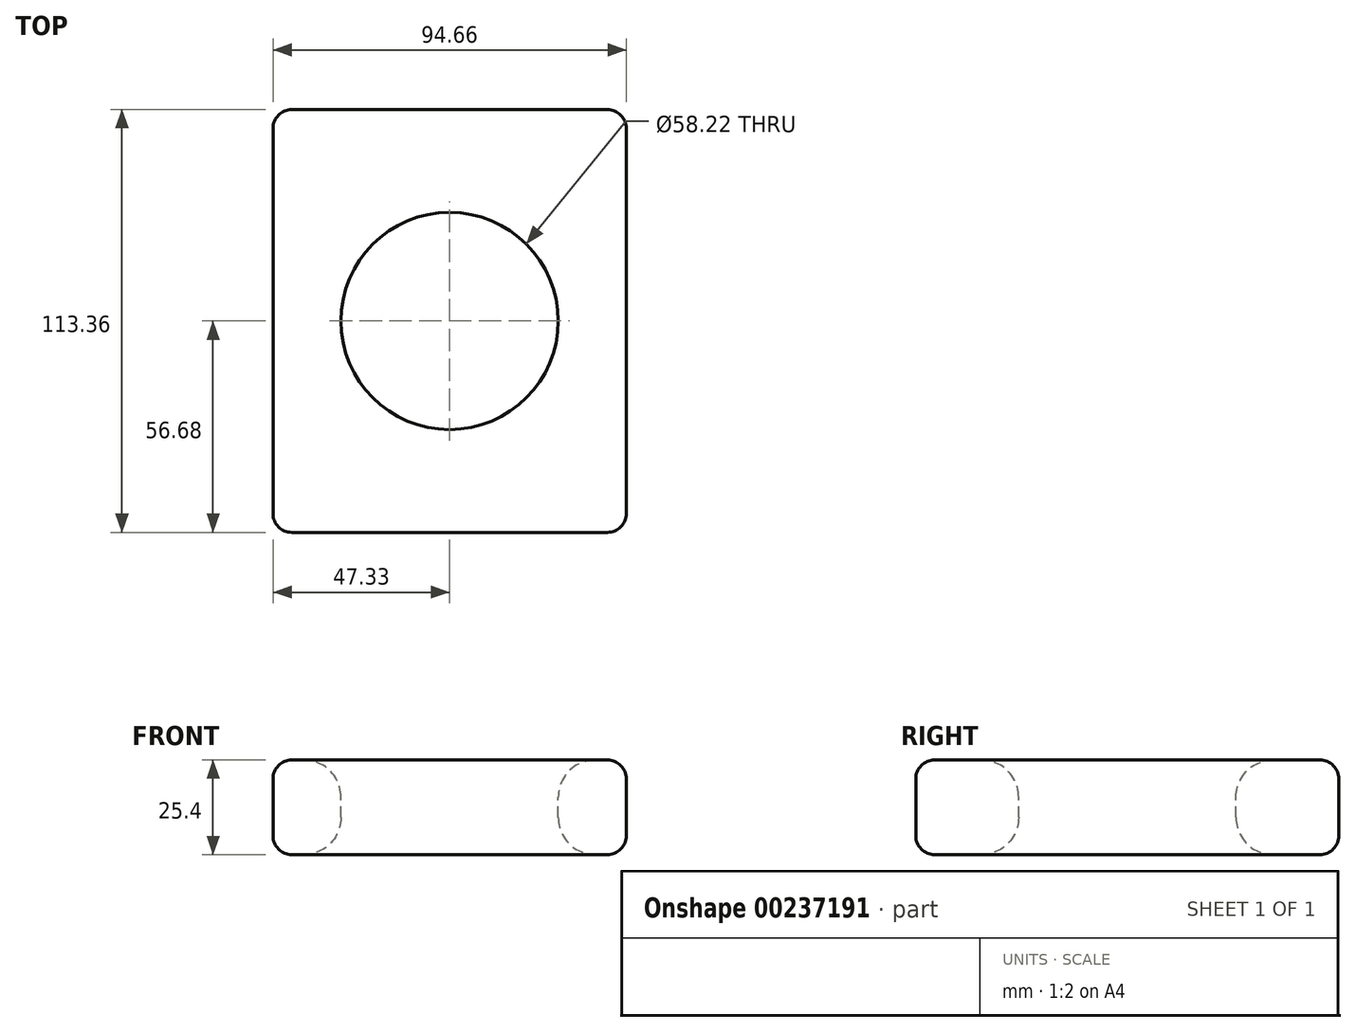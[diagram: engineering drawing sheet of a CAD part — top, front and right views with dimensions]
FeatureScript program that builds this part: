
annotation { "Feature Type Name" : "Feature", "Feature Type Description" : "" }
export const myFeature = defineFeature(function(context is Context, id is Id, definition is map)
    precondition{}
    {
        {
            var Q0;
            Q0=qCreatedBy(makeId("Top.planeOp"),FACE);
            var sketch = newSketch(context, id + "F0", { "sketchPlane" : qUnion([Q0])});
            skLineSegment(sketch, "E0.bottom", {"start": v(47.33, 56.68) * mm, "end": v(-47.33, 56.68) * mm});
            skLineSegment(sketch, "E0.top", {"start": v(47.33, -56.68) * mm, "end": v(-47.33, -56.68) * mm});
            skLineSegment(sketch, "E0.left", {"start": v(47.33, 56.68) * mm, "end": v(47.33, -56.68) * mm});
            skLineSegment(sketch, "E0.right", {"start": v(-47.33, 56.68) * mm, "end": v(-47.33, -56.68) * mm});
            skPoint(sketch, "E0.middle", {"position": v(0, 0) * mm});
            skSolve(sketch);
        }
        {
            var Q0;
            Q0=makeQuery(id+"F0.imprint","IMPRINT",FACE,{"disambiguationData":[TD([[makeQuery(id+"F0.imprint","IMPRINT",EDGE,{"derivedFrom":sQuery(id+"F0.wireOp",EDGE,"E0.bottom")}),1.0]])]});
            extrude(context, id + "F1", {"entities" : qUnion([Q0]), "depth" : 25.4 * mm});
        }
        {
            var Q0;
            Q0=makeQuery(id+"F1.opExtrude","CAP_FACE",FACE,{"disambiguationData":[OSD([sQuery(id+"F0.wireOp",EDGE,"E0.bottom"),sQuery(id+"F0.wireOp",EDGE,"E0.top"),sQuery(id+"F0.wireOp",EDGE,"E0.left"),sQuery(id+"F0.wireOp",EDGE,"E0.right")])],"isStart":false});
            var sketch = newSketch(context, id + "F2", { "sketchPlane" : qUnion([Q0])});
            skCircle(sketch, "E1", {"center": v(0, 0) * mm, "radius": 29.1 * mm});
            skSolve(sketch);
        }
        {
            var Q0;
            Q0 = qSketchRegion(id + "F2", true);
            extrude(context, id + "F3", {"entities" : qUnion([Q0]), "operationType" : NewBodyOperationType.REMOVE, "endBound" : BoundingType.THROUGH_ALL, "oppositeDirection" : true, "depth" : 25.4 * mm});
        }
        {
            var Q0;
            Q0=makeQuery(id+"F1.opExtrude","SWEPT_FACE",FACE,{"disambiguationData":[OSD([sQuery(id+"F0.wireOp",EDGE,"E0.top")])]});
            var Q1;
            Q1=makeQuery(id+"F1.opExtrude","SWEPT_FACE",FACE,{"disambiguationData":[OSD([sQuery(id+"F0.wireOp",EDGE,"E0.left")])]});
            var Q2;
            Q2=makeQuery(id+"F1.opExtrude","SWEPT_FACE",FACE,{"disambiguationData":[OSD([sQuery(id+"F0.wireOp",EDGE,"E0.bottom")])]});
            var Q3;
            Q3=makeQuery(id+"F1.opExtrude","SWEPT_FACE",FACE,{"disambiguationData":[OSD([sQuery(id+"F0.wireOp",EDGE,"E0.right")])]});
            fillet(context, id + "F4", {"entities" : qUnion([Q0, Q1, Q2, Q3]), "radius" : 5.08 * mm, "tangentPropagation" : true, "allowEdgeOverflow" : false});
        }
        {
            var Q0;
            Q0=makeQuery(id+"F3.boolean.opBoolean","COPY",FACE,{"derivedFrom":makeQuery(id+"F3.opExtrude","SWEPT_FACE",FACE,{"disambiguationData":[OSD([sQuery(id+"F2.wireOp",EDGE,"E1")])]})});
            fillet(context, id + "F5", {"entities" : qUnion([Q0]), "radius" : 10 * mm, "tangentPropagation" : true, "allowEdgeOverflow" : false});
        }
    });
